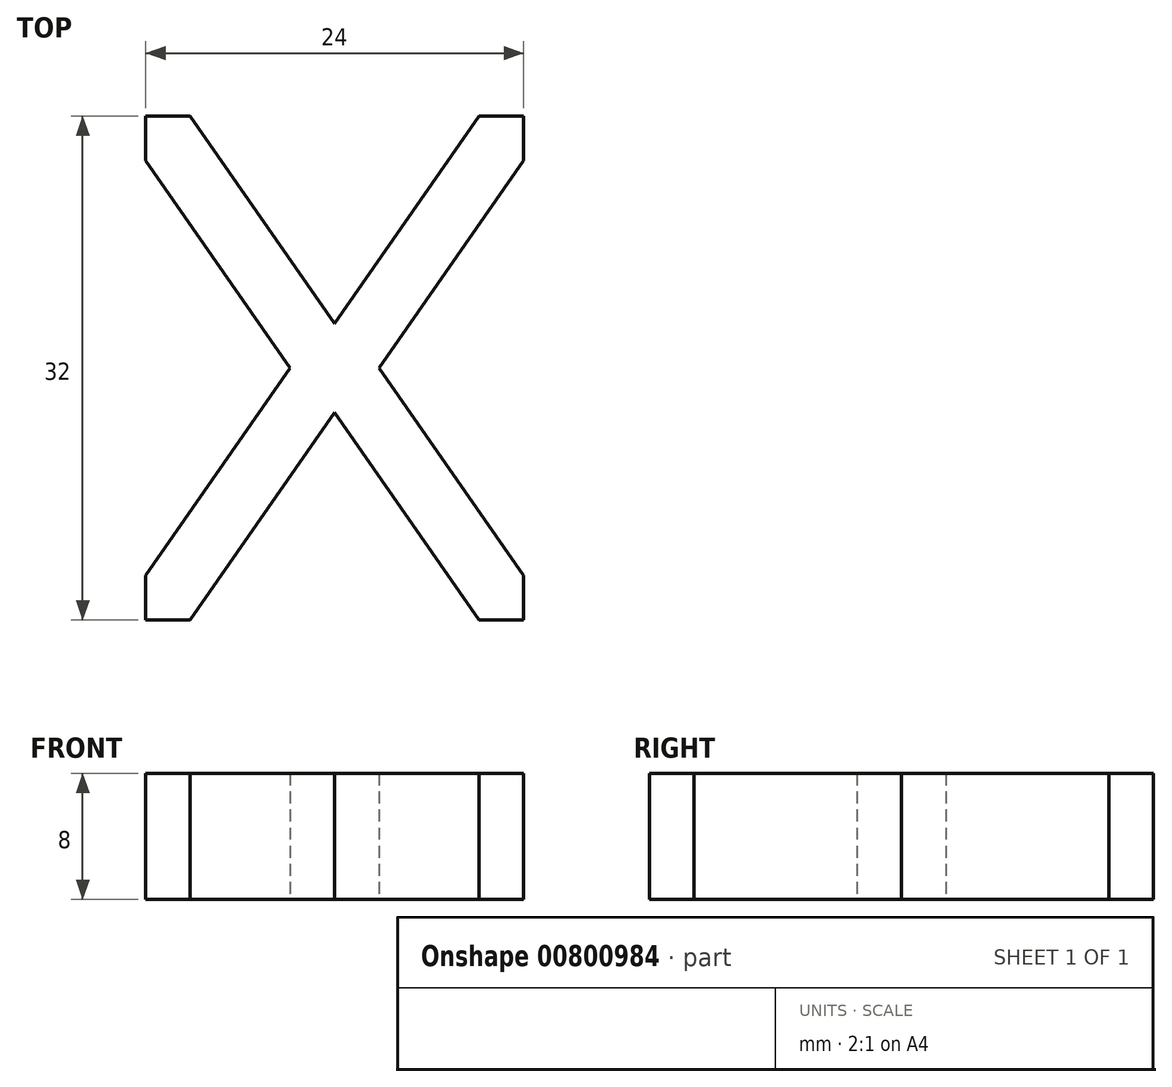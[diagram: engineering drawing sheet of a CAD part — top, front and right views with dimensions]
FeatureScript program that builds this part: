
annotation { "Feature Type Name" : "Feature", "Feature Type Description" : "" }
export const myFeature = defineFeature(function(context is Context, id is Id, definition is map)
    precondition{}
    {
        {
            var Q0;
            Q0=qCreatedBy(makeId("Top.planeOp"),FACE);
            var sketch = newSketch(context, id + "F0", { "sketchPlane" : qUnion([Q0])});
            skLineSegment(sketch, "E0", {"start": v(0, 0) * mm, "end": v(2.83, 0) * mm});
            skLineSegment(sketch, "E1", {"start": v(2.83, 0) * mm, "end": v(12, -13.17) * mm});
            skLineSegment(sketch, "E2", {"start": v(12, -13.17) * mm, "end": v(21.17, 0) * mm});
            skLineSegment(sketch, "E3", {"start": v(21.17, 0) * mm, "end": v(24, 0) * mm});
            skLineSegment(sketch, "E4", {"start": v(24, 0) * mm, "end": v(24, -2.83) * mm});
            skLineSegment(sketch, "E5", {"start": v(24, -2.83) * mm, "end": v(14.83, -16) * mm});
            skLineSegment(sketch, "E6", {"start": v(14.83, -16) * mm, "end": v(24, -29.17) * mm});
            skLineSegment(sketch, "E7", {"start": v(24, -29.17) * mm, "end": v(24, -32) * mm});
            skLineSegment(sketch, "E8", {"start": v(24, -32) * mm, "end": v(21.17, -32) * mm});
            skLineSegment(sketch, "E9", {"start": v(21.17, -32) * mm, "end": v(12, -18.83) * mm});
            skLineSegment(sketch, "E10", {"start": v(12, -18.83) * mm, "end": v(2.83, -32) * mm});
            skLineSegment(sketch, "E11", {"start": v(2.83, -32) * mm, "end": v(0, -32) * mm});
            skLineSegment(sketch, "E12", {"start": v(0, -32) * mm, "end": v(0, -29.17) * mm});
            skLineSegment(sketch, "E13", {"start": v(0, -29.17) * mm, "end": v(9.17, -16) * mm});
            skLineSegment(sketch, "E14", {"start": v(9.17, -16) * mm, "end": v(0, -2.83) * mm});
            skLineSegment(sketch, "E15", {"start": v(0, -2.83) * mm, "end": v(0, 0) * mm});
            skSolve(sketch);
        }
        {
            var Q0;
            Q0=makeQuery(id+"F0.imprint","IMPRINT",FACE,{"disambiguationData":[TD([[makeQuery(id+"F0.imprint","IMPRINT",EDGE,{"derivedFrom":sQuery(id+"F0.wireOp",EDGE,"E0")}),-1.0]])]});
            extrude(context, id + "F1", {"entities" : qUnion([Q0]), "depth" : 8 * mm, "offsetDistance" : 25 * mm});
        }
    });
